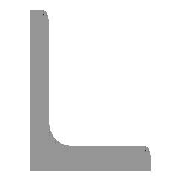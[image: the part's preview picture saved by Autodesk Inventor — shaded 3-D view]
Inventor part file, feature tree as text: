
AUTODESK INVENTOR PART (.ipt)
format: ipt  version: 2013 (Build 170138000, 138)  size: 130,560 bytes
history: native  units: mm (DEFAULTED — no unit token found)
features: other x4, plane x3, split x2, sketch x2
ambient origin geometry x8: Origin, YZ Plane, XZ Plane, XY Plane, X Axis, Y Axis, Z Axis, Center Point
bodies: Solid1 (feature_tree), Body (feature_tree)
feature tree (11):
  parser-record x1  (decoder bookkeeping rows leaked as tree rows — omitted from the tree; the rows remain in map.json)
  other  "Driven Length"
  other  "Start plane"
  other  "End plane"
  plane  "Work Plane4"
  split  "Split1"
  plane  "Work Plane5"
  split  "Split2"
  sketch  "Sketch3"  dims[d0=38.1mm]
  plane  "Work Plane3"
  sketch  "Sketch4"  dims[d1=38.1mm d2=4.7625mm d3=4.7625mm d4=1231.9mm d5=0.0mm d10=0.0mm d11=0.0mm d12=-0.0mm d13=1231.9mm d14=4.826mm d15=2.286mm d16=90.0deg d17=1231.9mm]
